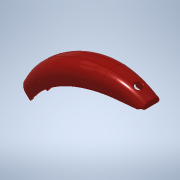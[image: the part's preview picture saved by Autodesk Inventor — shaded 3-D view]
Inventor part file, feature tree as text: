
AUTODESK INVENTOR PART (.ipt)
format: ipt  version: 2020 (Build 240168000, 168)  size: 8,019,968 bytes
history: native  units: in
note: dims shown in document units (in); Inventor stores cm internally (conversion verified against a paired STEP export)
features: fillet x14, sketch x12, extrude x10, delete_face x4, revolve x4, other x3, sweep x1, draft x1, mirror x1, boolean_combine x1, chamfer x1, split x1
ambient origin geometry x8: Origin, YZ Plane, XZ Plane, XY Plane, X Axis, Y Axis, Z Axis, Center Point
bodies: Solid5 (feature_tree), Solid6 (feature_tree)
feature tree (53):
  other  "Part1b1.ipt"
  extrude  "Extrusion1"  Depth=1.1in
  sketch  "Sketch3-<F>"  dims[d7=0.78in d8=1.1in]
  sketch  "Sketch6-<F>"  dims[d10=1.0in d13=2.75in d14=0.975in d15=0.26in d16=0.405in d17=0.725in]
  sketch  "3D Sketch2"
  sweep  "Sweep3"
  delete_face  "Delete Face22"
  delete_face  "Delete Face23"
  draft  "FaceDraft1"
  mirror  "Mirror2"
  fillet  "Fillet12"  Radius=0.975in
  fillet  "Fillet13"  Radius=0.26in
  delete_face  "Delete Face24"
  delete_face  "Delete Face25"
  fillet  "Fillet14"  Radius=0.405in
  fillet  "Fillet15"  Radius=0.725in
  extrude  "Extrusion2"  Depth=2.695in
  fillet  "Fillet16"  Radius=0.268in
  fillet  "Fillet17"  Radius=0.12in
  fillet  "Fillet18"  Radius=0.3in
  boolean_combine  "Combine3"
  extrude  "Extrusion5"  Depth=1.035in
  fillet  "Fillet19"  Radius=0.18in
  sketch  "Sketch8-<F>"  dims[d18=0.625in d19=2.695in d20=0.268in d21=0.12in d22=0.3in d23=-0.0687in]
  extrude  "Extrusion3"  Depth=0.7in
  extrude  "Extrusion4"  Depth=1.15in
  chamfer  "Chamfer1"  Distance=0.145in
  sketch  "Sketch11-<F>"  dims[d25=0.78in d26=1.035in d30=0.18in]
  extrude  "Extrusion6"  Depth=0.01in
  fillet  "Fillet21"  Radius=0.09in
  extrude  "Extrusion7"  Depth=0.01in
  fillet  "Fillet25"  Radius=0.35in
  fillet  "Fillet26"  Radius=0.75in
  fillet  "Fillet22"  Radius=0.075in
  split  "Split2"
  sketch  "Sketch14-<F>"  dims[d31=0.475in d32=0.7in]
  revolve  "Revolution1"  [1 undecoded]
  revolve  "Revolution2"  [1 undecoded]
  revolve  "Revolution3"  [1 undecoded]
  revolve  "Revolution4"  [1 undecoded]
  fillet  "Fillet24"  Radius=0.03in
  sketch  "Sketch15-<F>"  dims[d33=0.975in d34=1.15in]
  extrude  "Extrusion11"  Depth=0.01in
  extrude  "Extrusion12"  Depth=0.01in
  fillet  "Fillet23"  Radius=0.225in
  extrude  "Extrusion13"  Depth=0.01in
  sketch  "Sketch2-<F>"  dims[d35=1.3in]
  sketch  "Sketch7-<F>"  dims[d36=0.1in]
  other  "Solid1::Part1b1.ipt"
  other  "TaggingFeature1"
  sketch  "Sketch9-<F>"  dims[d37=0.112in]
  sketch  "Sketch10-<F>"  dims[d38=0.14in]
  sketch  "Sketch16-<F>"  dims[d39=0.15in d40=0.145in d41=0.125in d42=0.09in d53=0.0412in d54=0.35in d55=0.75in d56=0.075in d57=0.425in d58=0.0in d59=0.0in d60=0.4947in d61=0.375in d62=0.03in d63=0.065in d107=0.0687in d108=0.225in d109=0.5in d110=0.625in d111=0.3937in d112=0.64in d113=0.0in d114=0.45in d115=0.1969in d116=0.7in d117=0.1969in d118=0.475in d119=0.3in d120=0.55in d121=0.1722in d122=0.08in d123=0.06in d124=0.125in d125=0.3937in d126=0.08in d127=0.06in d128=0.125in d129=0.3937in d130=0.045in d131=0.09in d132=0.115in d133=0.2461in d134=0.045in d135=0.09in d136=0.115in d137=0.2541in d139=0.052in d140=0.06in d141=0.198in d142=0.2554in d143=0.0in d144=0.008in d145=0.02in d146=0.03in d147=0.143in d148=0.1755in d149=0.023in d150=0.1in d151=0.008in d152=0.125in d153=0.108in d154=0.03in d155=0.3937in d156=0.101in d157=1.0in d158=0.0in d159=0.136in d160=0.0in d161=0.019in d162=0.016in d163=45.0deg d167=1.1501in d168=0.268in d169=1.512in d170=0.5in d171=0.7in d172=0.03in d173=0.03in d174=0.03in d175=0.166in d176=0.0in d177=0.01in d178=0.198in d179=0.2745in d180=0.5in d184=0.2752in d185=0.0in d187=0.0118in d188=0.0in d198=0.008in d199=0.008in d209=0.009in d210=0.009in d231=0.327in d232=1.264in d233=0.1271in d234=0.2474in d237=0.01in d238=0.01in d239=0.25in d240=90.0deg d241=90.0deg d242=0.1465in d243=0.055in d244=0.04in d245=0.03in d246=0.052in d247=0.1168in d248=0.04in d249=0.024in d250=0.052in d251=0.1168in d252=90.0deg d253=90.0deg d254=0.317in d255=0.237in d256=0.0363in d257=1.0915in d258=0.0225in d259=0.1571in d260=0.0in d261=0.075in d262=0.045in d263=0.235in d264=0.0in d265=0.01in d266=0.03in d267=0.0in d268=0.7578in d269=0.15in d270=0.0748in d271=0.0748in d273=0.0787in d274=0.189in d278=0.0098in d284=0.2559in d285=0.0276in d286=0.0in d287=0.1535in d288=0.0374in d289=0.0079in d290=0.0059in]
note: 4 required parameter values undecoded (feature->parameter linkage not recoverable at this tier; creation-order binding heuristic only, values carry confidence <= 0.55)
